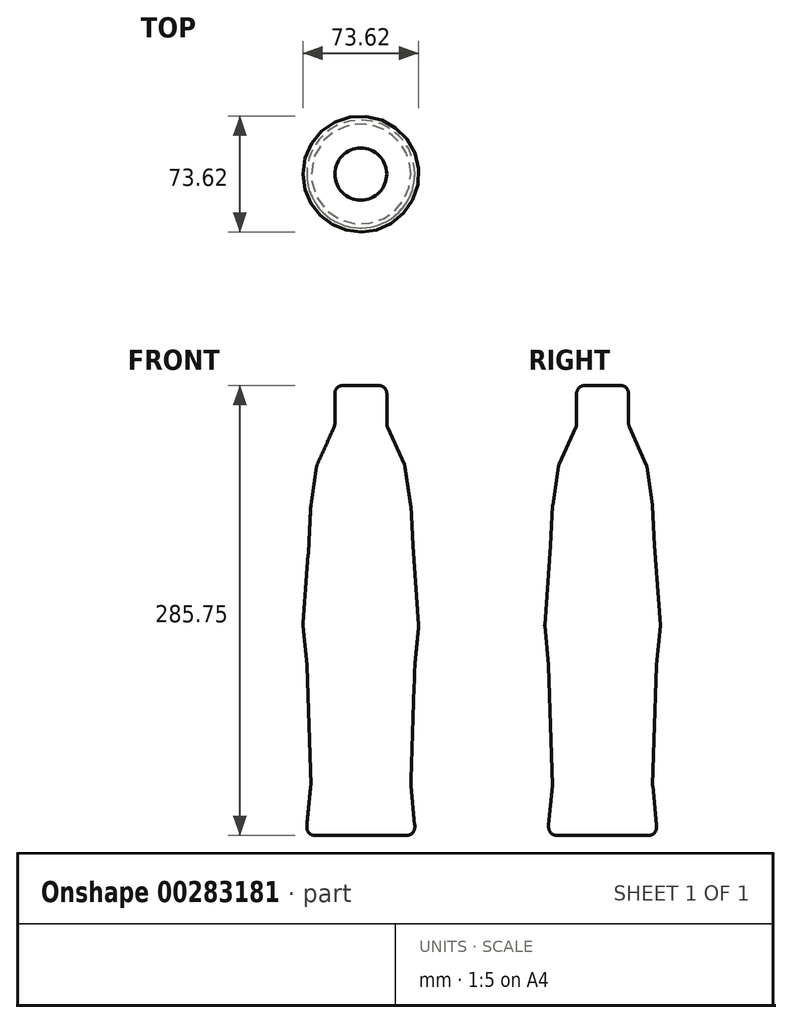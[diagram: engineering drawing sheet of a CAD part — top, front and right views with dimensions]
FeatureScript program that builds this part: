
annotation { "Feature Type Name" : "Feature", "Feature Type Description" : "" }
export const myFeature = defineFeature(function(context is Context, id is Id, definition is map)
    precondition{}
    {
        {
            var Q0;
            Q0=qCreatedBy(makeId("Top.planeOp"),FACE);
            cPlane(context, id + "F0", {"entities" : qUnion([Q0]), "cplaneType" : CPlaneType.OFFSET, "offset" : 6.35 * mm, "width" : 152.4 * mm, "height" : 152.4 * mm});
        }
        {
            var Q0;
            Q0=qCreatedBy(id+"F0.planeOp",FACE);
            cPlane(context, id + "F1", {"entities" : qUnion([Q0]), "cplaneType" : CPlaneType.OFFSET, "offset" : 25.4 * mm, "width" : 152.4 * mm, "height" : 152.4 * mm});
        }
        {
            var Q0;
            Q0=qCreatedBy(id+"F1.planeOp",FACE);
            cPlane(context, id + "F2", {"entities" : qUnion([Q0]), "cplaneType" : CPlaneType.OFFSET, "offset" : 76.2 * mm, "width" : 152.4 * mm, "height" : 152.4 * mm});
        }
        {
            var Q0;
            Q0=qCreatedBy(id+"F2.planeOp",FACE);
            cPlane(context, id + "F3", {"entities" : qUnion([Q0]), "cplaneType" : CPlaneType.OFFSET, "offset" : 25.4 * mm, "width" : 152.4 * mm, "height" : 152.4 * mm});
        }
        {
            var Q0;
            Q0=qCreatedBy(id+"F3.planeOp",FACE);
            cPlane(context, id + "F4", {"entities" : qUnion([Q0]), "cplaneType" : CPlaneType.OFFSET, "offset" : 25.4 * mm, "width" : 152.4 * mm, "height" : 152.4 * mm});
        }
        {
            var Q0;
            Q0=qCreatedBy(id+"F4.planeOp",FACE);
            cPlane(context, id + "F5", {"entities" : qUnion([Q0]), "cplaneType" : CPlaneType.OFFSET, "offset" : 25.4 * mm, "width" : 152.4 * mm, "height" : 152.4 * mm});
        }
        {
            var Q0;
            Q0=qCreatedBy(id+"F5.planeOp",FACE);
            cPlane(context, id + "F6", {"entities" : qUnion([Q0]), "cplaneType" : CPlaneType.OFFSET, "offset" : 25.4 * mm, "width" : 152.4 * mm, "height" : 152.4 * mm});
        }
        {
            var Q0;
            Q0=qCreatedBy(id+"F6.planeOp",FACE);
            cPlane(context, id + "F7", {"entities" : qUnion([Q0]), "cplaneType" : CPlaneType.OFFSET, "offset" : 25.4 * mm, "width" : 152.4 * mm, "height" : 152.4 * mm});
        }
        {
            var Q0;
            Q0=qCreatedBy(id+"F7.planeOp",FACE);
            cPlane(context, id + "F8", {"entities" : qUnion([Q0]), "cplaneType" : CPlaneType.OFFSET, "offset" : 25.4 * mm, "width" : 152.4 * mm, "height" : 152.4 * mm});
        }
        {
            var Q0;
            Q0=qCreatedBy(id+"F8.planeOp",FACE);
            cPlane(context, id + "F9", {"entities" : qUnion([Q0]), "cplaneType" : CPlaneType.OFFSET, "offset" : 25.4 * mm, "width" : 152.4 * mm, "height" : 152.4 * mm});
        }
        {
            var Q0;
            Q0=qCreatedBy(makeId("Top.planeOp"),FACE);
            var sketch = newSketch(context, id + "F10", { "sketchPlane" : qUnion([Q0])});
            skCircle(sketch, "E0", {"center": v(0, 0) * mm, "radius": 34.3 * mm});
            skSolve(sketch);
        }
        {
            var Q0;
            Q0=qCreatedBy(id+"F0.planeOp",FACE);
            var sketch = newSketch(context, id + "F11", { "sketchPlane" : qUnion([Q0])});
            skCircle(sketch, "E1", {"center": v(0, 0) * mm, "radius": 34.3 * mm});
            skSolve(sketch);
        }
        {
            var Q0;
            Q0=qCreatedBy(id+"F1.planeOp",FACE);
            var sketch = newSketch(context, id + "F12", { "sketchPlane" : qUnion([Q0])});
            skCircle(sketch, "E2", {"center": v(0, 0) * mm, "radius": 31.75 * mm});
            skSolve(sketch);
        }
        {
            var Q0;
            Q0=qCreatedBy(id+"F2.planeOp",FACE);
            var sketch = newSketch(context, id + "F13", { "sketchPlane" : qUnion([Q0])});
            skCircle(sketch, "E3", {"center": v(0, 0) * mm, "radius": 34.3 * mm});
            skSolve(sketch);
        }
        {
            var Q0;
            Q0=qCreatedBy(id+"F3.planeOp",FACE);
            var sketch = newSketch(context, id + "F14", { "sketchPlane" : qUnion([Q0])});
            skCircle(sketch, "E4", {"center": v(0, 0) * mm, "radius": 36.83 * mm});
            skSolve(sketch);
        }
        {
            var Q0;
            Q0=qCreatedBy(id+"F5.planeOp",FACE);
            var sketch = newSketch(context, id + "F15", { "sketchPlane" : qUnion([Q0])});
            skCircle(sketch, "E5", {"center": v(0, 0) * mm, "radius": 33.02 * mm});
            skSolve(sketch);
        }
        {
            var Q0;
            Q0=qCreatedBy(id+"F6.planeOp",FACE);
            var sketch = newSketch(context, id + "F16", { "sketchPlane" : qUnion([Q0])});
            skCircle(sketch, "E6", {"center": v(0, 0) * mm, "radius": 31.75 * mm});
            skSolve(sketch);
        }
        {
            var Q0;
            Q0=qCreatedBy(id+"F7.planeOp",FACE);
            var sketch = newSketch(context, id + "F17", { "sketchPlane" : qUnion([Q0])});
            skCircle(sketch, "E7", {"center": v(0, 0) * mm, "radius": 27.94 * mm});
            skSolve(sketch);
        }
        {
            var Q0;
            Q0=qCreatedBy(id+"F8.planeOp",FACE);
            var sketch = newSketch(context, id + "F18", { "sketchPlane" : qUnion([Q0])});
            skCircle(sketch, "E8", {"center": v(0, 0) * mm, "radius": 16.51 * mm});
            skSolve(sketch);
        }
        {
            var Q0;
            Q0=qCreatedBy(id+"F9.planeOp",FACE);
            var sketch = newSketch(context, id + "F19", { "sketchPlane" : qUnion([Q0])});
            skCircle(sketch, "E9", {"center": v(0, 0) * mm, "radius": 16.51 * mm});
            skSolve(sketch);
        }
        {
            var Q0;
            Q0=makeQuery(id+"F11.imprint","IMPRINT",FACE,{"disambiguationData":[TD([[makeQuery(id+"F11.imprint","IMPRINT",EDGE,{"derivedFrom":sQuery(id+"F11.wireOp",EDGE,"E1")}),1.0]])]});
            var Q1;
            Q1=makeQuery(id+"F10.imprint","IMPRINT",FACE,{"disambiguationData":[TD([[makeQuery(id+"F10.imprint","IMPRINT",EDGE,{"derivedFrom":sQuery(id+"F10.wireOp",EDGE,"E0")}),1.0]])]});
            loft(context, id + "F20", {"sheetProfilesArray" : [{ "sheetProfileEntities" : qUnion([Q0]) }, { "sheetProfileEntities" : qUnion([Q1]) }]});
        }
        {
            var Q1;
            Q1=makeQuery(id+"F20.opLoft","CAP_FACE",FACE,{"disambiguationData":[OSD([makeQuery(id+"F11.imprint","IMPRINT",FACE,{"disambiguationData":[TD([[makeQuery(id+"F11.imprint","IMPRINT",EDGE,{"derivedFrom":sQuery(id+"F11.wireOp",EDGE,"E1")}),1.0]])]})])],"isStart":true});
            var Q2;
            Q2=makeQuery(id+"F12.imprint","IMPRINT",FACE,{"disambiguationData":[TD([[makeQuery(id+"F12.imprint","IMPRINT",EDGE,{"derivedFrom":sQuery(id+"F12.wireOp",EDGE,"E2")}),1.0]])]});
            loft(context, id + "F21", {"operationType" : NewBodyOperationType.ADD, "sheetProfilesArray" : [{ "sheetProfileEntities" : qUnion([Q1]) }, { "sheetProfileEntities" : qUnion([Q2]) }]});
        }
        {
            var Q1;
            Q1=makeQuery(id+"F21.opLoft","CAP_FACE",FACE,{"disambiguationData":[OSD([makeQuery(id+"F12.imprint","IMPRINT",FACE,{"disambiguationData":[TD([[makeQuery(id+"F12.imprint","IMPRINT",EDGE,{"derivedFrom":sQuery(id+"F12.wireOp",EDGE,"E2")}),1.0]])]})])],"isStart":true});
            var Q2;
            Q2=makeQuery(id+"F13.imprint","IMPRINT",FACE,{"disambiguationData":[TD([[makeQuery(id+"F13.imprint","IMPRINT",EDGE,{"derivedFrom":sQuery(id+"F13.wireOp",EDGE,"E3")}),1.0]])]});
            loft(context, id + "F22", {"operationType" : NewBodyOperationType.ADD, "sheetProfilesArray" : [{ "sheetProfileEntities" : qUnion([Q1]) }, { "sheetProfileEntities" : qUnion([Q2]) }]});
        }
        {
            var Q1;
            Q1=makeQuery(id+"F22.opLoft","CAP_FACE",FACE,{"disambiguationData":[OSD([makeQuery(id+"F13.imprint","IMPRINT",FACE,{"disambiguationData":[TD([[makeQuery(id+"F13.imprint","IMPRINT",EDGE,{"derivedFrom":sQuery(id+"F13.wireOp",EDGE,"E3")}),1.0]])]})])],"isStart":true});
            var Q2;
            Q2=makeQuery(id+"F14.imprint","IMPRINT",FACE,{"disambiguationData":[TD([[makeQuery(id+"F14.imprint","IMPRINT",EDGE,{"derivedFrom":sQuery(id+"F14.wireOp",EDGE,"E4")}),1.0]])]});
            loft(context, id + "F23", {"operationType" : NewBodyOperationType.ADD, "sheetProfilesArray" : [{ "sheetProfileEntities" : qUnion([Q1]) }, { "sheetProfileEntities" : qUnion([Q2]) }]});
        }
        {
            var Q1;
            Q1=makeQuery(id+"F23.opLoft","CAP_FACE",FACE,{"disambiguationData":[OSD([makeQuery(id+"F14.imprint","IMPRINT",FACE,{"disambiguationData":[TD([[makeQuery(id+"F14.imprint","IMPRINT",EDGE,{"derivedFrom":sQuery(id+"F14.wireOp",EDGE,"E4")}),1.0]])]})])],"isStart":true});
            var Q2;
            Q2=makeQuery(id+"F15.imprint","IMPRINT",FACE,{"disambiguationData":[TD([[makeQuery(id+"F15.imprint","IMPRINT",EDGE,{"derivedFrom":sQuery(id+"F15.wireOp",EDGE,"E5")}),1.0]])]});
            loft(context, id + "F24", {"operationType" : NewBodyOperationType.ADD, "sheetProfilesArray" : [{ "sheetProfileEntities" : qUnion([Q1]) }, { "sheetProfileEntities" : qUnion([Q2]) }]});
        }
        {
            var Q1;
            Q1=makeQuery(id+"F24.opLoft","CAP_FACE",FACE,{"disambiguationData":[OSD([makeQuery(id+"F15.imprint","IMPRINT",FACE,{"disambiguationData":[TD([[makeQuery(id+"F15.imprint","IMPRINT",EDGE,{"derivedFrom":sQuery(id+"F15.wireOp",EDGE,"E5")}),1.0]])]})])],"isStart":true});
            var Q2;
            Q2=makeQuery(id+"F16.imprint","IMPRINT",FACE,{"disambiguationData":[TD([[makeQuery(id+"F16.imprint","IMPRINT",EDGE,{"derivedFrom":sQuery(id+"F16.wireOp",EDGE,"E6")}),1.0]])]});
            loft(context, id + "F25", {"operationType" : NewBodyOperationType.ADD, "sheetProfilesArray" : [{ "sheetProfileEntities" : qUnion([Q1]) }, { "sheetProfileEntities" : qUnion([Q2]) }]});
        }
        {
            var Q1;
            Q1=makeQuery(id+"F25.opLoft","CAP_FACE",FACE,{"disambiguationData":[OSD([makeQuery(id+"F16.imprint","IMPRINT",FACE,{"disambiguationData":[TD([[makeQuery(id+"F16.imprint","IMPRINT",EDGE,{"derivedFrom":sQuery(id+"F16.wireOp",EDGE,"E6")}),1.0]])]})])],"isStart":true});
            var Q2;
            Q2=makeQuery(id+"F17.imprint","IMPRINT",FACE,{"disambiguationData":[TD([[makeQuery(id+"F17.imprint","IMPRINT",EDGE,{"derivedFrom":sQuery(id+"F17.wireOp",EDGE,"E7")}),1.0]])]});
            loft(context, id + "F26", {"operationType" : NewBodyOperationType.ADD, "sheetProfilesArray" : [{ "sheetProfileEntities" : qUnion([Q1]) }, { "sheetProfileEntities" : qUnion([Q2]) }]});
        }
        {
            var Q1;
            Q1=makeQuery(id+"F26.opLoft","CAP_FACE",FACE,{"disambiguationData":[OSD([makeQuery(id+"F17.imprint","IMPRINT",FACE,{"disambiguationData":[TD([[makeQuery(id+"F17.imprint","IMPRINT",EDGE,{"derivedFrom":sQuery(id+"F17.wireOp",EDGE,"E7")}),1.0]])]})])],"isStart":true});
            var Q2;
            Q2=makeQuery(id+"F18.imprint","IMPRINT",FACE,{"disambiguationData":[TD([[makeQuery(id+"F18.imprint","IMPRINT",EDGE,{"derivedFrom":sQuery(id+"F18.wireOp",EDGE,"E8")}),1.0]])]});
            loft(context, id + "F27", {"operationType" : NewBodyOperationType.ADD, "sheetProfilesArray" : [{ "sheetProfileEntities" : qUnion([Q1]) }, { "sheetProfileEntities" : qUnion([Q2]) }]});
        }
        {
            var Q1;
            Q1=makeQuery(id+"F27.opLoft","CAP_FACE",FACE,{"disambiguationData":[OSD([makeQuery(id+"F18.imprint","IMPRINT",FACE,{"disambiguationData":[TD([[makeQuery(id+"F18.imprint","IMPRINT",EDGE,{"derivedFrom":sQuery(id+"F18.wireOp",EDGE,"E8")}),1.0]])]})])],"isStart":true});
            var Q2;
            Q2=makeQuery(id+"F19.imprint","IMPRINT",FACE,{"disambiguationData":[TD([[makeQuery(id+"F19.imprint","IMPRINT",EDGE,{"derivedFrom":sQuery(id+"F19.wireOp",EDGE,"E9")}),1.0]])]});
            loft(context, id + "F28", {"operationType" : NewBodyOperationType.ADD, "sheetProfilesArray" : [{ "sheetProfileEntities" : qUnion([Q1]) }, { "sheetProfileEntities" : qUnion([Q2]) }]});
        }
        {
            var Q0;
            Q0=makeQuery(id+"F20.opLoft","MID_CAP_EDGE",EDGE,{"disambiguationData":[OSD([sQuery(id+"F10.wireOp",EDGE,"E0"),sQuery(id+"F11.wireOp",EDGE,"E1")])],"capPos":1.0});
            var Q1;
            {var subQ0=sQuery(id+"F11.wireOp",EDGE,"E1");Q1=makeQuery(id+"F21.boolean.opBoolean","MERGE",EDGE,{"derivedFrom":[makeQuery(id+"F20.opLoft","MID_CAP_EDGE",EDGE,{"disambiguationData":[OSD([subQ0])],"capPos":0.0}),makeQuery(id+"F21.opLoft","MID_CAP_EDGE",EDGE,{"disambiguationData":[OSD([subQ0])],"capPos":0.0})]});}
            var Q2;
            {var subQ0=sQuery(id+"F12.wireOp",EDGE,"E2");var subQ1=sQuery(id+"F11.wireOp",EDGE,"E1");Q2=makeQuery(id+"F22.boolean.opBoolean","MERGE",EDGE,{"derivedFrom":[makeQuery(id+"F21.opLoft","MID_CAP_EDGE",EDGE,{"disambiguationData":[OSD([subQ1,subQ0])],"capPos":1.0}),makeQuery(id+"F22.opLoft","MID_CAP_EDGE",EDGE,{"disambiguationData":[OSD([subQ1,subQ0])],"capPos":0.0})]});}
            var Q3;
            {var subQ0=sQuery(id+"F13.wireOp",EDGE,"E3");var subQ1=sQuery(id+"F12.wireOp",EDGE,"E2");var subQ2=sQuery(id+"F11.wireOp",EDGE,"E1");Q3=makeQuery(id+"F23.boolean.opBoolean","MERGE",EDGE,{"derivedFrom":[makeQuery(id+"F22.opLoft","MID_CAP_EDGE",EDGE,{"disambiguationData":[OSD([subQ2,subQ1,subQ0])],"capPos":1.0}),makeQuery(id+"F23.opLoft","MID_CAP_EDGE",EDGE,{"disambiguationData":[OSD([subQ2,subQ1,subQ0])],"capPos":0.0})]});}
            var Q4;
            {var subQ0=sQuery(id+"F14.wireOp",EDGE,"E4");var subQ1=sQuery(id+"F13.wireOp",EDGE,"E3");var subQ2=sQuery(id+"F12.wireOp",EDGE,"E2");var subQ3=sQuery(id+"F11.wireOp",EDGE,"E1");Q4=makeQuery(id+"F24.boolean.opBoolean","MERGE",EDGE,{"derivedFrom":[makeQuery(id+"F23.opLoft","MID_CAP_EDGE",EDGE,{"disambiguationData":[OSD([subQ3,subQ2,subQ1,subQ0])],"capPos":1.0}),makeQuery(id+"F24.opLoft","MID_CAP_EDGE",EDGE,{"disambiguationData":[OSD([subQ3,subQ2,subQ1,subQ0])],"capPos":0.0})]});}
            var Q5;
            {var subQ0=sQuery(id+"F15.wireOp",EDGE,"E5");var subQ1=sQuery(id+"F14.wireOp",EDGE,"E4");var subQ2=sQuery(id+"F13.wireOp",EDGE,"E3");var subQ3=sQuery(id+"F12.wireOp",EDGE,"E2");var subQ4=sQuery(id+"F11.wireOp",EDGE,"E1");Q5=makeQuery(id+"F25.boolean.opBoolean","MERGE",EDGE,{"derivedFrom":[makeQuery(id+"F24.opLoft","MID_CAP_EDGE",EDGE,{"disambiguationData":[OSD([subQ4,subQ3,subQ2,subQ1,subQ0])],"capPos":1.0}),makeQuery(id+"F25.opLoft","MID_CAP_EDGE",EDGE,{"disambiguationData":[OSD([subQ4,subQ3,subQ2,subQ1,subQ0])],"capPos":0.0})]});}
            var Q6;
            Q6=makeQuery(id+"F25.opLoft","SWEPT_FACE",FACE,{"disambiguationData":[OSD([sQuery(id+"F11.wireOp",EDGE,"E1"),sQuery(id+"F12.wireOp",EDGE,"E2"),sQuery(id+"F13.wireOp",EDGE,"E3"),sQuery(id+"F14.wireOp",EDGE,"E4"),sQuery(id+"F15.wireOp",EDGE,"E5"),sQuery(id+"F16.wireOp",EDGE,"E6")])]});
            var Q7;
            {var subQ0=sQuery(id+"F17.wireOp",EDGE,"E7");var subQ1=sQuery(id+"F16.wireOp",EDGE,"E6");var subQ2=sQuery(id+"F15.wireOp",EDGE,"E5");var subQ3=sQuery(id+"F14.wireOp",EDGE,"E4");var subQ4=sQuery(id+"F13.wireOp",EDGE,"E3");var subQ5=sQuery(id+"F12.wireOp",EDGE,"E2");var subQ6=sQuery(id+"F11.wireOp",EDGE,"E1");Q7=makeQuery(id+"F27.boolean.opBoolean","MERGE",EDGE,{"derivedFrom":[makeQuery(id+"F26.opLoft","MID_CAP_EDGE",EDGE,{"disambiguationData":[OSD([subQ6,subQ5,subQ4,subQ3,subQ2,subQ1,subQ0])],"capPos":1.0}),makeQuery(id+"F27.opLoft","MID_CAP_EDGE",EDGE,{"disambiguationData":[OSD([subQ6,subQ5,subQ4,subQ3,subQ2,subQ1,subQ0])],"capPos":0.0})]});}
            var Q8;
            {var subQ0=sQuery(id+"F18.wireOp",EDGE,"E8");var subQ1=sQuery(id+"F17.wireOp",EDGE,"E7");var subQ2=sQuery(id+"F16.wireOp",EDGE,"E6");var subQ3=sQuery(id+"F15.wireOp",EDGE,"E5");var subQ4=sQuery(id+"F14.wireOp",EDGE,"E4");var subQ5=sQuery(id+"F13.wireOp",EDGE,"E3");var subQ6=sQuery(id+"F12.wireOp",EDGE,"E2");var subQ7=sQuery(id+"F11.wireOp",EDGE,"E1");Q8=makeQuery(id+"F28.boolean.opBoolean","MERGE",EDGE,{"derivedFrom":[makeQuery(id+"F27.opLoft","MID_CAP_EDGE",EDGE,{"disambiguationData":[OSD([subQ7,subQ6,subQ5,subQ4,subQ3,subQ2,subQ1,subQ0])],"capPos":1.0}),makeQuery(id+"F28.opLoft","MID_CAP_EDGE",EDGE,{"disambiguationData":[OSD([subQ7,subQ6,subQ5,subQ4,subQ3,subQ2,subQ1,subQ0])],"capPos":0.0})]});}
            var Q9;
            Q9=makeQuery(id+"F28.opLoft","MID_CAP_EDGE",EDGE,{"disambiguationData":[OSD([sQuery(id+"F11.wireOp",EDGE,"E1"),sQuery(id+"F12.wireOp",EDGE,"E2"),sQuery(id+"F13.wireOp",EDGE,"E3"),sQuery(id+"F14.wireOp",EDGE,"E4"),sQuery(id+"F15.wireOp",EDGE,"E5"),sQuery(id+"F16.wireOp",EDGE,"E6"),sQuery(id+"F17.wireOp",EDGE,"E7"),sQuery(id+"F18.wireOp",EDGE,"E8"),sQuery(id+"F19.wireOp",EDGE,"E9")])],"capPos":1.0});
            fillet(context, id + "F29", {"entities" : qUnion([Q0, Q1, Q2, Q3, Q4, Q5, Q6, Q7, Q8, Q9]), "radius" : 5.08 * mm, "tangentPropagation" : true, "allowEdgeOverflow" : false});
        }
    });
